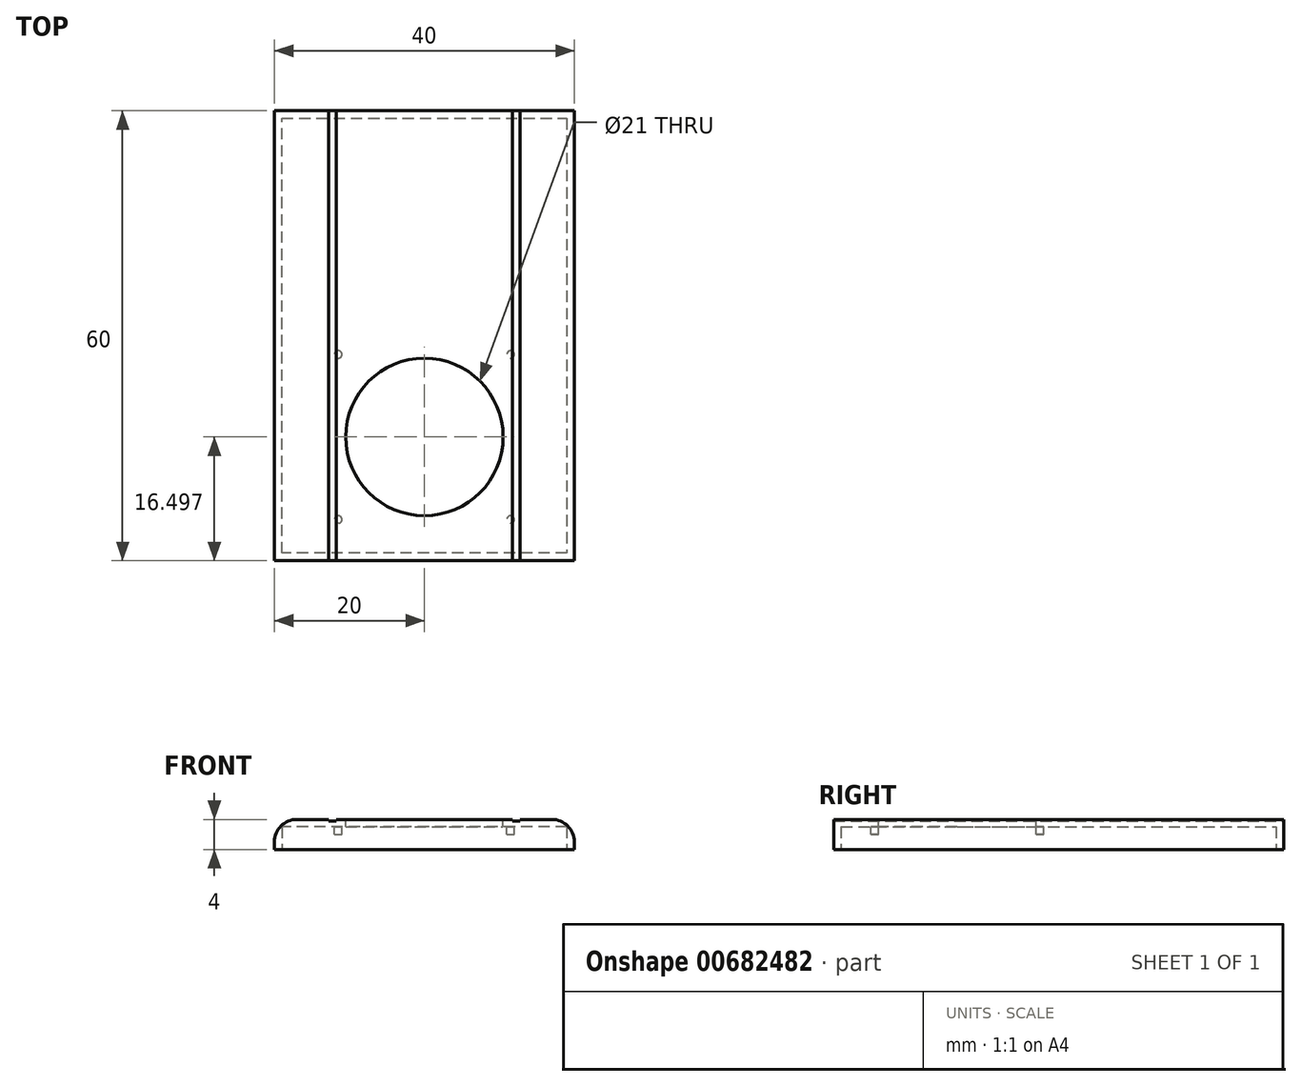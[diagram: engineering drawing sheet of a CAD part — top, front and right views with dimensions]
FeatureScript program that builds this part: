
annotation { "Feature Type Name" : "Feature", "Feature Type Description" : "" }
export const myFeature = defineFeature(function(context is Context, id is Id, definition is map)
    precondition{}
    {
        {
            var Q0;
            Q0=qCreatedBy(makeId("Top.planeOp"),FACE);
            var sketch = newSketch(context, id + "F0", { "sketchPlane" : qUnion([Q0])});
            skLineSegment(sketch, "E0.bottom", {"start": v(-20, 33.19) * mm, "end": v(20, 33.19) * mm});
            skLineSegment(sketch, "E0.top", {"start": v(-20, -26.81) * mm, "end": v(20, -26.81) * mm});
            skLineSegment(sketch, "E0.left", {"start": v(-20, 33.19) * mm, "end": v(-20, -26.81) * mm});
            skLineSegment(sketch, "E0.right", {"start": v(20, 33.19) * mm, "end": v(20, -26.81) * mm});
            skPoint(sketch, "E0.middle", {"position": v(0, 3.19) * mm});
            skSolve(sketch);
        }
        {
            var Q0;
            Q0 = qSketchRegion(id + "F0", true);
            extrude(context, id + "F1", {"entities" : qUnion([Q0]), "depth" : 4 * mm, "offsetDistance" : 25 * mm});
        }
        {
            var Q0;
            Q0=makeQuery(id+"F1.opExtrude","CAP_FACE",FACE,{"disambiguationData":[OSD([sQuery(id+"F0.wireOp",EDGE,"E0.bottom"),sQuery(id+"F0.wireOp",EDGE,"E0.top"),sQuery(id+"F0.wireOp",EDGE,"E0.left"),sQuery(id+"F0.wireOp",EDGE,"E0.right")])],"isStart":false});
            var sketch = newSketch(context, id + "F2", { "sketchPlane" : qUnion([Q0])});
            skLineSegment(sketch, "E1", {"start": v(0, -26.81) * mm, "end": v(11.75, -26.81) * mm});
            skLineSegment(sketch, "E2", {"start": v(0, -26.81) * mm, "end": v(-11.75, -26.81) * mm});
            skLineSegment(sketch, "E3", {"start": v(-11.75, -26.81) * mm, "end": v(-11.75, 33.19) * mm});
            skLineSegment(sketch, "E4", {"start": v(11.75, -26.81) * mm, "end": v(11.75, 33.19) * mm});
            skLineSegment(sketch, "E5", {"start": v(-11.75, -26.81) * mm, "end": v(-12.75, -26.81) * mm});
            skLineSegment(sketch, "E6", {"start": v(11.75, -26.81) * mm, "end": v(12.75, -26.81) * mm});
            skLineSegment(sketch, "E7", {"start": v(-12.75, -26.81) * mm, "end": v(-12.75, 33.19) * mm});
            skLineSegment(sketch, "E8", {"start": v(12.75, -26.81) * mm, "end": v(12.75, 33.19) * mm});
            skLineSegment(sketch, "E9", {"start": v(-12.75, 33.19) * mm, "end": v(12.75, 33.19) * mm});
            skSolve(sketch);
        }
        {
            var Q0;
            {var subQ0=sQuery(id+"F2.wireOp",EDGE,"E3");Q0=makeQuery(id+"F2.imprint","IMPRINT",FACE,{"disambiguationData":[TD([[makeQuery(id+"F2.imprint","IMPRINT",EDGE,{"derivedFrom":subQ0}),1.0]])]});}
            var Q1;
            {var subQ0=sQuery(id+"F2.wireOp",EDGE,"E4");Q1=makeQuery(id+"F2.imprint","IMPRINT",FACE,{"disambiguationData":[TD([[makeQuery(id+"F2.imprint","IMPRINT",EDGE,{"derivedFrom":subQ0}),-1.0]])]});}
            extrude(context, id + "F3", {"entities" : qUnion([Q0, Q1]), "operationType" : NewBodyOperationType.REMOVE, "oppositeDirection" : true, "depth" : .25 * mm, "offsetDistance" : 25 * mm});
        }
        {
            var Q0;
            Q0=makeQuery(id+"F1.opExtrude","CAP_EDGE",EDGE,{"disambiguationData":[OSD([sQuery(id+"F0.wireOp",EDGE,"E0.left")])],"isStart":false});
            var Q1;
            Q1=makeQuery(id+"F1.opExtrude","CAP_EDGE",EDGE,{"disambiguationData":[OSD([sQuery(id+"F0.wireOp",EDGE,"E0.right")])],"isStart":false});
            fillet(context, id + "F4", {"entities" : qUnion([Q0, Q1]), "radius" : 3 * mm, "tangentPropagation" : true, "allowEdgeOverflow" : false});
        }
        {
            var Q0;
            {var subQ0=sQuery(id+"F0.wireOp",EDGE,"E0.bottom");var subQ1=sQuery(id+"F0.wireOp",EDGE,"E0.top");Q0=makeQuery(id+"F3.boolean.opBoolean","SPLIT",FACE,{"disambiguationData":[TD([makeQuery(id+"F3.opExtrude","SWEPT_FACE",FACE,{"disambiguationData":[OSD([sQuery(id+"F2.wireOp",EDGE,"E3")])]})])],"derivedFrom":makeQuery(id+"F1.opExtrude","CAP_FACE",FACE,{"disambiguationData":[OSD([subQ0,subQ1,sQuery(id+"F0.wireOp",EDGE,"E0.left"),sQuery(id+"F0.wireOp",EDGE,"E0.right")])],"isStart":false})});}
            var sketch = newSketch(context, id + "F5", { "sketchPlane" : qUnion([Q0])});
            skLineSegment(sketch, "E10", {"start": v(0, -26.81) * mm, "end": v(0, -10.31) * mm});
            skCircle(sketch, "E11", {"center": v(0, -10.31) * mm, "radius": 10.5 * mm});
            skSolve(sketch);
        }
        {
            var Q0;
            Q0 = qSketchRegion(id + "F5", true);
            extrude(context, id + "F6", {"entities" : qUnion([Q0]), "operationType" : NewBodyOperationType.REMOVE, "oppositeDirection" : true, "depth" : 25 * mm, "offsetDistance" : 25 * mm});
        }
        {
            var Q0;
            Q0=makeQuery(id+"F1.opExtrude","CAP_FACE",FACE,{"disambiguationData":[OSD([sQuery(id+"F0.wireOp",EDGE,"E0.bottom"),sQuery(id+"F0.wireOp",EDGE,"E0.top"),sQuery(id+"F0.wireOp",EDGE,"E0.left"),sQuery(id+"F0.wireOp",EDGE,"E0.right")])],"isStart":true});
            var sketch = newSketch(context, id + "F7", { "sketchPlane" : qUnion([Q0])});
            skLineSegment(sketch, "E12.0", {"start": v(-19, 25.81) * mm, "end": v(-19, -32.19) * mm});
            skLineSegment(sketch, "E12.1", {"start": v(19, 25.81) * mm, "end": v(-19, 25.81) * mm});
            skLineSegment(sketch, "E12.2", {"start": v(19, -32.19) * mm, "end": v(19, 25.81) * mm});
            skLineSegment(sketch, "E12.3", {"start": v(-19, -32.19) * mm, "end": v(19, -32.19) * mm});
            skSolve(sketch);
        }
        {
            var Q0;
            Q0 = qSketchRegion(id + "F7", true);
            extrude(context, id + "F8", {"entities" : qUnion([Q0]), "operationType" : NewBodyOperationType.REMOVE, "oppositeDirection" : true, "depth" : 3 * mm, "offsetDistance" : 25 * mm});
        }
        {
            var Q0;
            Q0=makeQuery(id+"F8.boolean.opBoolean","COPY",FACE,{"derivedFrom":makeQuery(id+"F8.opExtrude","CAP_FACE",FACE,{"disambiguationData":[OSD([sQuery(id+"F7.wireOp",EDGE,"E12.0"),sQuery(id+"F7.wireOp",EDGE,"E12.1"),sQuery(id+"F7.wireOp",EDGE,"E12.2"),sQuery(id+"F7.wireOp",EDGE,"E12.3")])],"isStart":false})});
            var sketch = newSketch(context, id + "F9", { "sketchPlane" : qUnion([Q0])});
            skLineSegment(sketch, "E13.bottom", {"start": v(11.5, 21.31) * mm, "end": v(-11.5, 21.31) * mm});
            skLineSegment(sketch, "E13.top", {"start": v(11.5, -0.69) * mm, "end": v(-11.5, -0.69) * mm});
            skLineSegment(sketch, "E13.left", {"start": v(11.5, 21.31) * mm, "end": v(11.5, -0.69) * mm});
            skLineSegment(sketch, "E13.right", {"start": v(-11.5, 21.31) * mm, "end": v(-11.5, -0.69) * mm});
            skPoint(sketch, "E13.middle", {"position": v(0, 10.31) * mm});
            skCircle(sketch, "E14", {"center": v(11.5, -0.69) * mm, "radius": 0.5 * mm});
            skCircle(sketch, "E15", {"center": v(11.5, 21.31) * mm, "radius": 0.5 * mm});
            skCircle(sketch, "E16", {"center": v(-11.5, -0.69) * mm, "radius": 0.5 * mm});
            skCircle(sketch, "E17", {"center": v(-11.5, 21.31) * mm, "radius": 0.5 * mm});
            skSolve(sketch);
        }
        {
            var Q0;
            {var subQ0=sQuery(id+"F9.wireOp",EDGE,"E13.left");var subQ1=sQuery(id+"F9.wireOp",EDGE,"E13.bottom");var subQ2=makeQuery(id+"F9.imprint","INTERSECT",VERTEX,{"derivedFrom":[subQ1,subQ0]});Q0=makeQuery(id+"F9.imprint","IMPRINT",FACE,{"disambiguationData":[TD([[makeQuery(id+"F9.imprint","IMPRINT",EDGE,{"disambiguationData":[TD([[subQ2,-1.0]])],"derivedFrom":subQ1}),1.0]])]});}
            var Q1;
            {var subQ0=sQuery(id+"F9.wireOp",EDGE,"E13.left");var subQ1=sQuery(id+"F9.wireOp",EDGE,"E13.bottom");var subQ2=makeQuery(id+"F9.imprint","INTERSECT",VERTEX,{"derivedFrom":[subQ1,subQ0]});Q1=makeQuery(id+"F9.imprint","IMPRINT",FACE,{"disambiguationData":[TD([[makeQuery(id+"F9.imprint","IMPRINT",EDGE,{"disambiguationData":[TD([[subQ2,-1.0]])],"derivedFrom":subQ1}),-1.0]])]});}
            var Q2;
            {var subQ0=sQuery(id+"F9.wireOp",EDGE,"E13.right");var subQ1=sQuery(id+"F9.wireOp",EDGE,"E13.bottom");var subQ2=makeQuery(id+"F9.imprint","INTERSECT",VERTEX,{"derivedFrom":[subQ1,subQ0]});Q2=makeQuery(id+"F9.imprint","IMPRINT",FACE,{"disambiguationData":[TD([[makeQuery(id+"F9.imprint","IMPRINT",EDGE,{"disambiguationData":[TD([[subQ2,1.0]])],"derivedFrom":subQ1}),-1.0]])]});}
            var Q3;
            {var subQ0=sQuery(id+"F9.wireOp",EDGE,"E13.right");var subQ1=sQuery(id+"F9.wireOp",EDGE,"E13.bottom");var subQ2=makeQuery(id+"F9.imprint","INTERSECT",VERTEX,{"derivedFrom":[subQ1,subQ0]});Q3=makeQuery(id+"F9.imprint","IMPRINT",FACE,{"disambiguationData":[TD([[makeQuery(id+"F9.imprint","IMPRINT",EDGE,{"disambiguationData":[TD([[subQ2,1.0]])],"derivedFrom":subQ1}),1.0]])]});}
            var Q4;
            {var subQ0=sQuery(id+"F9.wireOp",EDGE,"E13.left");var subQ1=sQuery(id+"F9.wireOp",EDGE,"E13.top");var subQ2=makeQuery(id+"F9.imprint","INTERSECT",VERTEX,{"derivedFrom":[subQ1,subQ0]});Q4=makeQuery(id+"F9.imprint","IMPRINT",FACE,{"disambiguationData":[TD([[makeQuery(id+"F9.imprint","IMPRINT",EDGE,{"disambiguationData":[TD([[subQ2,-1.0]])],"derivedFrom":subQ1}),-1.0]])]});}
            var Q5;
            {var subQ0=sQuery(id+"F9.wireOp",EDGE,"E13.left");var subQ1=sQuery(id+"F9.wireOp",EDGE,"E13.top");var subQ2=makeQuery(id+"F9.imprint","INTERSECT",VERTEX,{"derivedFrom":[subQ1,subQ0]});Q5=makeQuery(id+"F9.imprint","IMPRINT",FACE,{"disambiguationData":[TD([[makeQuery(id+"F9.imprint","IMPRINT",EDGE,{"disambiguationData":[TD([[subQ2,-1.0]])],"derivedFrom":subQ1}),1.0]])]});}
            var Q6;
            {var subQ0=sQuery(id+"F9.wireOp",EDGE,"E13.right");var subQ1=sQuery(id+"F9.wireOp",EDGE,"E13.top");var subQ2=makeQuery(id+"F9.imprint","INTERSECT",VERTEX,{"derivedFrom":[subQ1,subQ0]});Q6=makeQuery(id+"F9.imprint","IMPRINT",FACE,{"disambiguationData":[TD([[makeQuery(id+"F9.imprint","IMPRINT",EDGE,{"disambiguationData":[TD([[subQ2,1.0]])],"derivedFrom":subQ1}),-1.0]])]});}
            var Q7;
            {var subQ0=sQuery(id+"F9.wireOp",EDGE,"E13.right");var subQ1=sQuery(id+"F9.wireOp",EDGE,"E13.top");var subQ2=makeQuery(id+"F9.imprint","INTERSECT",VERTEX,{"derivedFrom":[subQ1,subQ0]});Q7=makeQuery(id+"F9.imprint","IMPRINT",FACE,{"disambiguationData":[TD([[makeQuery(id+"F9.imprint","IMPRINT",EDGE,{"disambiguationData":[TD([[subQ2,1.0]])],"derivedFrom":subQ1}),1.0]])]});}
            extrude(context, id + "F10", {"entities" : qUnion([Q0, Q1, Q2, Q3, Q4, Q5, Q6, Q7]), "operationType" : NewBodyOperationType.ADD, "depth" : 1 * mm, "offsetDistance" : 25 * mm});
        }
    });
